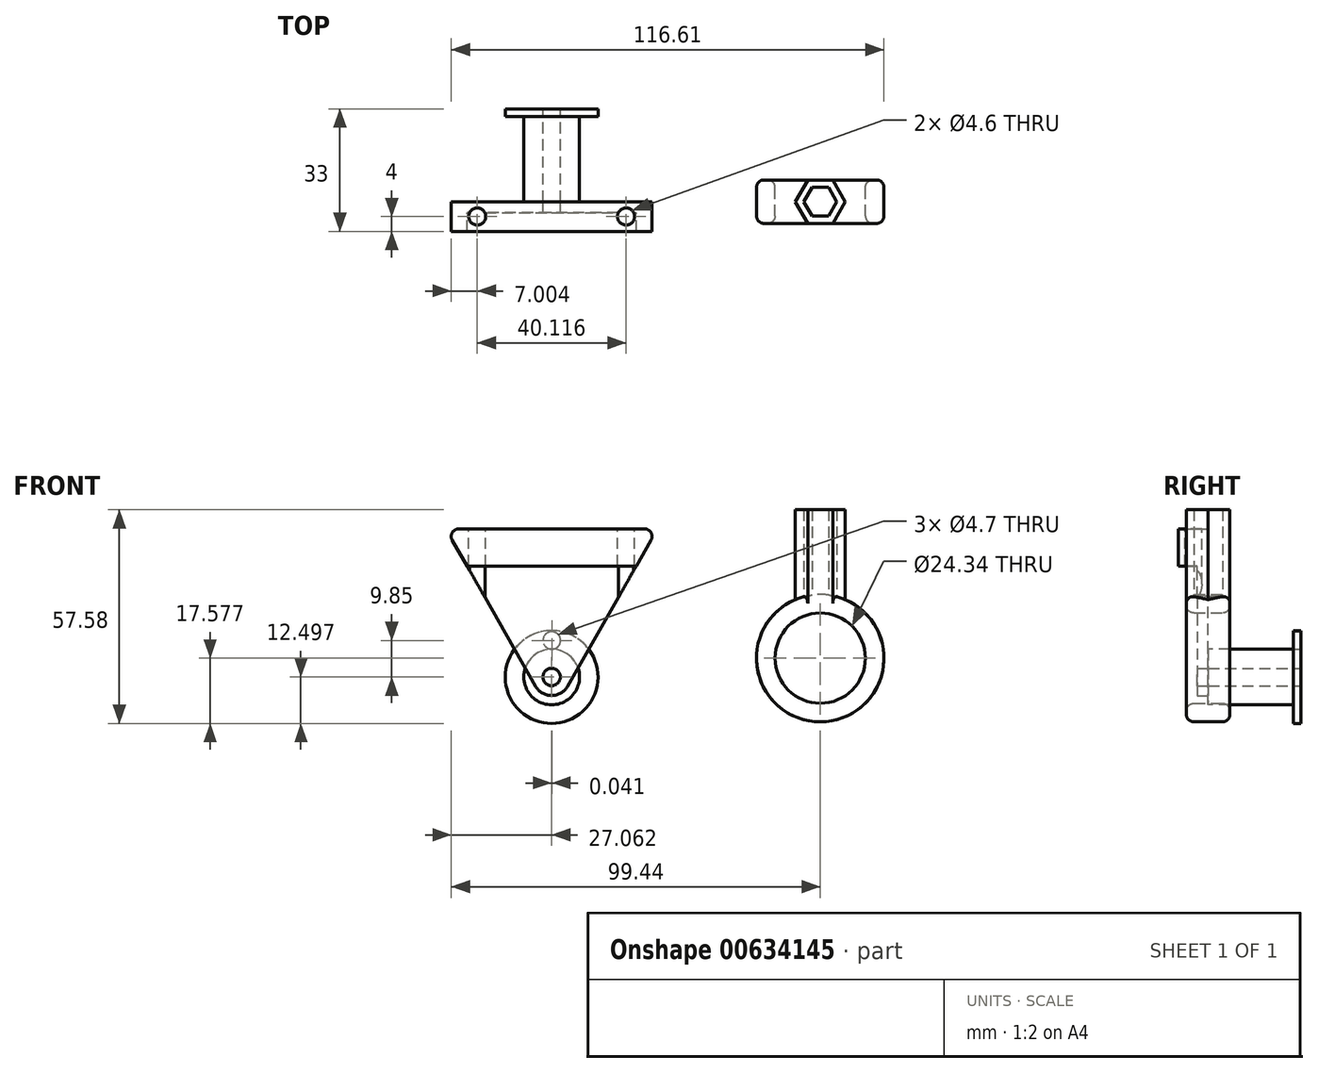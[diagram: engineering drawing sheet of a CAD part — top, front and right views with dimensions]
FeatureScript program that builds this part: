
annotation { "Feature Type Name" : "Feature", "Feature Type Description" : "" }
export const myFeature = defineFeature(function(context is Context, id is Id, definition is map)
    precondition{}
    {
        {
            var Q0;
            Q0=qCreatedBy(makeId("Top.planeOp"),FACE);
            var sketch = newSketch(context, id + "F0", { "sketchPlane" : qUnion([Q0])});
            skCircle(sketch, "E0.cCircle", {"center": v(0, 0) * mm, "radius": 3.85 * mm, "construction": true});
            skLineSegment(sketch, "E0.0", {"start": v(-2.22, 3.85) * mm, "end": v(2.22, 3.85) * mm});
            skLineSegment(sketch, "E0.1", {"start": v(2.22, 3.85) * mm, "end": v(4.45, 0) * mm});
            skLineSegment(sketch, "E0.2", {"start": v(4.45, 0) * mm, "end": v(2.22, -3.85) * mm});
            skLineSegment(sketch, "E0.3", {"start": v(2.22, -3.85) * mm, "end": v(-2.22, -3.85) * mm});
            skLineSegment(sketch, "E0.4", {"start": v(-2.22, -3.85) * mm, "end": v(-4.45, 0) * mm});
            skLineSegment(sketch, "E0.5", {"start": v(-4.45, 0) * mm, "end": v(-2.22, 3.85) * mm});
            skPoint(sketch, "E0.0.midPoint", {"position": v(0, 3.85) * mm});
            skCircle(sketch, "E1.cCircle", {"center": v(0, 0) * mm, "radius": 5.85 * mm, "construction": true});
            skLineSegment(sketch, "E1.0", {"start": v(-3.38, 5.85) * mm, "end": v(3.38, 5.85) * mm});
            skLineSegment(sketch, "E1.1", {"start": v(3.38, 5.85) * mm, "end": v(6.75, 0) * mm});
            skLineSegment(sketch, "E1.2", {"start": v(6.75, 0) * mm, "end": v(3.38, -5.85) * mm});
            skLineSegment(sketch, "E1.3", {"start": v(3.38, -5.85) * mm, "end": v(-3.38, -5.85) * mm});
            skLineSegment(sketch, "E1.4", {"start": v(-3.38, -5.85) * mm, "end": v(-6.75, 0) * mm});
            skLineSegment(sketch, "E1.5", {"start": v(-6.75, 0) * mm, "end": v(-3.38, 5.85) * mm});
            skPoint(sketch, "E1.0.midPoint", {"position": v(0, 5.85) * mm});
            skSolve(sketch);
        }
        {
            var Q0;
            Q0=makeQuery(id+"F0.imprint","IMPRINT",FACE,{"disambiguationData":[TD([[makeQuery(id+"F0.imprint","IMPRINT",EDGE,{"derivedFrom":sQuery(id+"F0.wireOp",EDGE,"E0.0")}),1.0]])]});
            extrude(context, id + "F1", {"entities" : qUnion([Q0]), "depth" : 25 * mm, "offsetDistance" : 25 * mm});
        }
        {
            var Q0;
            Q0=qCreatedBy(makeId("Front.planeOp"),FACE);
            var sketch = newSketch(context, id + "F2", { "sketchPlane" : qUnion([Q0])});
            skCircle(sketch, "E2", {"center": v(0, -15) * mm, "radius": 17.17 * mm});
            skCircle(sketch, "E3", {"center": v(0, -15) * mm, "radius": 12.17 * mm});
            skSolve(sketch);
        }
        {
            var Q0;
            Q0=makeQuery(id+"F2.imprint","IMPRINT",FACE,{"disambiguationData":[TD([[makeQuery(id+"F2.imprint","IMPRINT",EDGE,{"derivedFrom":sQuery(id+"F2.wireOp",EDGE,"E2")}),1.0]])]});
            extrude(context, id + "F3", {"entities" : qUnion([Q0]), "operationType" : NewBodyOperationType.ADD, "endBound" : BoundingType.SYMMETRIC, "depth" : 11.7 * mm, "offsetDistance" : 25 * mm});
        }
        {
            var Q0;
            Q0=makeQuery(id+"F3.opExtrude","CAP_EDGE",EDGE,{"disambiguationData":[OSD([sQuery(id+"F2.wireOp",EDGE,"E3")])],"isStart":false});
            var Q1;
            Q1=makeQuery(id+"F3.opExtrude","CAP_EDGE",EDGE,{"disambiguationData":[OSD([sQuery(id+"F2.wireOp",EDGE,"E3")])],"isStart":true});
            var Q2;
            Q2=makeQuery(id+"F3.opExtrude","CAP_EDGE",EDGE,{"disambiguationData":[OSD([sQuery(id+"F2.wireOp",EDGE,"E2")])],"isStart":true});
            var Q3;
            Q3=makeQuery(id+"F3.opExtrude","CAP_EDGE",EDGE,{"disambiguationData":[OSD([sQuery(id+"F2.wireOp",EDGE,"E2")])],"isStart":false});
            fillet(context, id + "F4", {"entities" : qUnion([Q0, Q1, Q2, Q3]), "radius" : 2 * mm, "tangentPropagation" : true, "allowEdgeOverflow" : false});
        }
        {
            var Q0;
            Q0=qCreatedBy(makeId("Front.planeOp"),FACE);
            var sketch = newSketch(context, id + "F5", { "sketchPlane" : qUnion([Q0])});
            skLineSegment(sketch, "E4", {"start": v(-43.88, 19.82) * mm, "end": v(-100.88, 19.82) * mm});
            skLineSegment(sketch, "E5", {"start": v(-100.88, 19.82) * mm, "end": v(-72.38, -30.18) * mm});
            skLineSegment(sketch, "E6", {"start": v(-72.38, -30.18) * mm, "end": v(-43.88, 19.82) * mm});
            skSolve(sketch);
        }
        {
            var Q0;
            Q0=makeQuery(id+"F5.imprint","IMPRINT",FACE,{"disambiguationData":[TD([[makeQuery(id+"F5.imprint","IMPRINT",EDGE,{"derivedFrom":sQuery(id+"F5.wireOp",EDGE,"E4")}),1.0]])]});
            extrude(context, id + "F6", {"entities" : qUnion([Q0]), "depth" : 3 * mm, "offsetDistance" : 25 * mm});
        }
        {
            var Q0;
            Q0=makeQuery(id+"F6.opExtrude","SWEPT_EDGE",EDGE,{"disambiguationData":[OSD([sQuery(id+"F5.wireOp",EDGE,"E5"),sQuery(id+"F5.wireOp",EDGE,"E6")])]});
            fillet(context, id + "F7", {"entities" : qUnion([Q0]), "radius" : 5 * mm, "tangentPropagation" : true, "allowEdgeOverflow" : false});
        }
        {
            var Q0;
            Q0=makeQuery(id+"F6.opExtrude","SWEPT_EDGE",EDGE,{"disambiguationData":[OSD([sQuery(id+"F5.wireOp",EDGE,"E4"),sQuery(id+"F5.wireOp",EDGE,"E6")])]});
            var Q1;
            Q1=makeQuery(id+"F6.opExtrude","SWEPT_EDGE",EDGE,{"disambiguationData":[OSD([sQuery(id+"F5.wireOp",EDGE,"E4"),sQuery(id+"F5.wireOp",EDGE,"E5")])]});
            fillet(context, id + "F8", {"entities" : qUnion([Q0, Q1]), "radius" : 2 * mm, "tangentPropagation" : true, "allowEdgeOverflow" : false});
        }
        {
            var Q0;
            Q0=makeQuery(id+"F6.opExtrude","CAP_FACE",FACE,{"disambiguationData":[OSD([sQuery(id+"F5.wireOp",EDGE,"E4"),sQuery(id+"F5.wireOp",EDGE,"E5"),sQuery(id+"F5.wireOp",EDGE,"E6")])],"isStart":false});
            var sketch = newSketch(context, id + "F9", { "sketchPlane" : qUnion([Q0])});
            skLineSegment(sketch, "E7.0", {"start": v(-47.32, 19.82) * mm, "end": v(-97.44, 19.82) * mm});
            skArc(sketch, "E8.0", {"start": v(-45.58, 16.83) * mm, "mid": v(-45.6, 18.83) * mm, "end": v(-47.32, 19.82) * mm});
            skArc(sketch, "E9.0", {"start": v(-97.44, 19.82) * mm, "mid": v(-99.17, 18.83) * mm, "end": v(-99.17, 16.83) * mm});
            skLineSegment(sketch, "E10", {"start": v(-45.58, 16.83) * mm, "end": v(-49.58, 9.82) * mm});
            skLineSegment(sketch, "E11", {"start": v(-49.58, 9.82) * mm, "end": v(-95.18, 9.82) * mm});
            skLineSegment(sketch, "E12", {"start": v(-95.18, 9.82) * mm, "end": v(-99.17, 16.83) * mm});
            skSolve(sketch);
        }
        {
            var Q0;
            Q0=makeQuery(id+"F9.imprint","IMPRINT",FACE,{"disambiguationData":[TD([[makeQuery(id+"F9.imprint","IMPRINT",EDGE,{"derivedFrom":sQuery(id+"F9.wireOp",EDGE,"E7.0")}),1.0]])]});
            extrude(context, id + "F10", {"entities" : qUnion([Q0]), "operationType" : NewBodyOperationType.ADD, "depth" : 5 * mm, "offsetDistance" : 25 * mm});
        }
        {
            var Q0;
            Q0=makeQuery(id+"F10.boolean.opBoolean","MERGE",FACE,{"derivedFrom":[makeQuery(id+"F6.opExtrude","SWEPT_FACE",FACE,{"disambiguationData":[OSD([sQuery(id+"F5.wireOp",EDGE,"E4")])]}),makeQuery(id+"F10.opExtrude","SWEPT_FACE",FACE,{"disambiguationData":[OSD([sQuery(id+"F9.wireOp",EDGE,"E7.0")])]})]});
            var sketch = newSketch(context, id + "F11", { "sketchPlane" : qUnion([Q0])});
            skSolve(sketch);
        }
        {
            var Q0;
            {var subQ0=sQuery(id+"F5.wireOp",EDGE,"E4");Q0=makeQuery(id+"F11.imprint","IMPRINT",FACE,{"disambiguationData":[TD([[makeQuery(id+"F11.imprint","IMPRINT",EDGE,{"derivedFrom":makeQuery(id+"F6.opExtrude","CAP_EDGE",EDGE,{"disambiguationData":[OSD([subQ0])],"isStart":true})}),1.0]])]});}
            var sketch = newSketch(context, id + "F12", { "sketchPlane" : qUnion([Q0])});
            skCircle(sketch, "E13", {"center": v(-92.44, -4) * mm, "radius": 2.3 * mm});
            skCircle(sketch, "E14", {"center": v(-52.32, -4) * mm, "radius": 2.3 * mm});
            skLineSegment(sketch, "E15", {"start": v(-52.32, -4) * mm, "end": v(-92.44, -4) * mm, "construction": true});
            skSolve(sketch);
        }
        {
            var Q0;
            Q0 = qSketchRegion(id + "F12", true);
            extrude(context, id + "F13", {"entities" : qUnion([Q0]), "operationType" : NewBodyOperationType.REMOVE, "oppositeDirection" : true, "depth" : 25 * mm, "offsetDistance" : 25 * mm});
        }
        {
            var Q0;
            Q0=makeQuery(id+"F6.opExtrude","CAP_FACE",FACE,{"disambiguationData":[OSD([sQuery(id+"F5.wireOp",EDGE,"E4"),sQuery(id+"F5.wireOp",EDGE,"E5"),sQuery(id+"F5.wireOp",EDGE,"E6")])],"isStart":true});
            var sketch = newSketch(context, id + "F14", { "sketchPlane" : qUnion([Q0])});
            skCircle(sketch, "E16", {"center": v(72.38, -20.08) * mm, "radius": 2.35 * mm});
            skLineSegment(sketch, "E17", {"start": v(72.38, -20.08) * mm, "end": v(72.38, 19.82) * mm, "construction": true});
            skSolve(sketch);
        }
        {
            var Q0;
            Q0 = qSketchRegion(id + "F14", true);
            extrude(context, id + "F15", {"entities" : qUnion([Q0]), "operationType" : NewBodyOperationType.REMOVE, "endBound" : BoundingType.THROUGH_ALL, "oppositeDirection" : true, "depth" : 25 * mm, "offsetDistance" : 25 * mm});
        }
        {
            var Q0;
            Q0=makeQuery(id+"F6.opExtrude","CAP_FACE",FACE,{"disambiguationData":[OSD([sQuery(id+"F5.wireOp",EDGE,"E4"),sQuery(id+"F5.wireOp",EDGE,"E5"),sQuery(id+"F5.wireOp",EDGE,"E6")])],"isStart":true});
            var sketch = newSketch(context, id + "F16", { "sketchPlane" : qUnion([Q0])});
            skCircle(sketch, "E18", {"center": v(72.38, -20.08) * mm, "radius": 7.5 * mm});
            skSolve(sketch);
        }
        {
            var Q0;
            Q0 = qSketchRegion(id + "F16", true);
            extrude(context, id + "F17", {"entities" : qUnion([Q0]), "depth" : 25 * mm, "offsetDistance" : 25 * mm});
        }
        {
            var Q0;
            Q0=makeQuery(id+"F17.opExtrude","CAP_FACE",FACE,{"disambiguationData":[OSD([sQuery(id+"F16.wireOp",EDGE,"E18")])],"isStart":false});
            var sketch = newSketch(context, id + "F18", { "sketchPlane" : qUnion([Q0])});
            skCircle(sketch, "E19", {"center": v(72.38, -20.08) * mm, "radius": 12.5 * mm});
            skSolve(sketch);
        }
        {
            var Q0;
            Q0=makeQuery(id+"F18.imprint","IMPRINT",FACE,{"disambiguationData":[TD([[makeQuery(id+"F18.imprint","IMPRINT",EDGE,{"derivedFrom":sQuery(id+"F18.wireOp",EDGE,"E19")}),1.0]])]});
            extrude(context, id + "F19", {"entities" : qUnion([Q0]), "operationType" : NewBodyOperationType.ADD, "oppositeDirection" : true, "depth" : 2 * mm, "offsetDistance" : 25 * mm});
        }
        {
            var Q0;
            {var subQ0=sQuery(id+"F16.wireOp",EDGE,"E18");Q0=makeQuery(id+"F19.boolean.opBoolean","MERGE",FACE,{"derivedFrom":[makeQuery(id+"F17.opExtrude","CAP_FACE",FACE,{"disambiguationData":[OSD([subQ0])],"isStart":false}),makeQuery(id+"F19.opExtrude","CAP_FACE",FACE,{"disambiguationData":[OSD([subQ0,sQuery(id+"F18.wireOp",EDGE,"E19")])],"isStart":true})]});}
            var sketch = newSketch(context, id + "F20", { "sketchPlane" : qUnion([Q0])});
            skCircle(sketch, "E20.0", {"center": v(72.38, -20.08) * mm, "radius": 2.35 * mm});
            skSolve(sketch);
        }
        {
            var Q0;
            Q0=makeQuery(id+"F20.imprint","IMPRINT",FACE,{"disambiguationData":[TD([[makeQuery(id+"F20.imprint","IMPRINT",EDGE,{"derivedFrom":sQuery(id+"F20.wireOp",EDGE,"E20.0")}),1.0]])]});
            extrude(context, id + "F21", {"entities" : qUnion([Q0]), "operationType" : NewBodyOperationType.REMOVE, "endBound" : BoundingType.THROUGH_ALL, "oppositeDirection" : true, "depth" : 25 * mm, "offsetDistance" : 25 * mm});
        }
        {
            var Q0;
            {var subQ0=sQuery(id+"F16.wireOp",EDGE,"E18");Q0=makeQuery(id+"F19.boolean.opBoolean","MERGE",FACE,{"derivedFrom":[makeQuery(id+"F17.opExtrude","CAP_FACE",FACE,{"disambiguationData":[OSD([subQ0])],"isStart":false}),makeQuery(id+"F19.opExtrude","CAP_FACE",FACE,{"disambiguationData":[OSD([subQ0,sQuery(id+"F18.wireOp",EDGE,"E19")])],"isStart":true})]});}
            var sketch = newSketch(context, id + "F22", { "sketchPlane" : qUnion([Q0])});
            skCircle(sketch, "E21", {"center": v(72.34, -10.23) * mm, "radius": 2.35 * mm});
            skSolve(sketch);
        }
        {
            var Q0;
            Q0 = qSketchRegion(id + "F22", true);
            var Q1;
            Q1=makeQuery(id+"F19.opExtrude","CAP_FACE",FACE,{"disambiguationData":[OSD([sQuery(id+"F16.wireOp",EDGE,"E18"),sQuery(id+"F18.wireOp",EDGE,"E19")])],"isStart":false});
            extrude(context, id + "F23", {"entities" : qUnion([Q0]), "operationType" : NewBodyOperationType.REMOVE, "endBound" : BoundingType.UP_TO_SURFACE, "oppositeDirection" : true, "depth" : 25 * mm, "endBoundEntityFace" : qUnion([Q1]), "offsetDistance" : 25 * mm});
        }
    });
